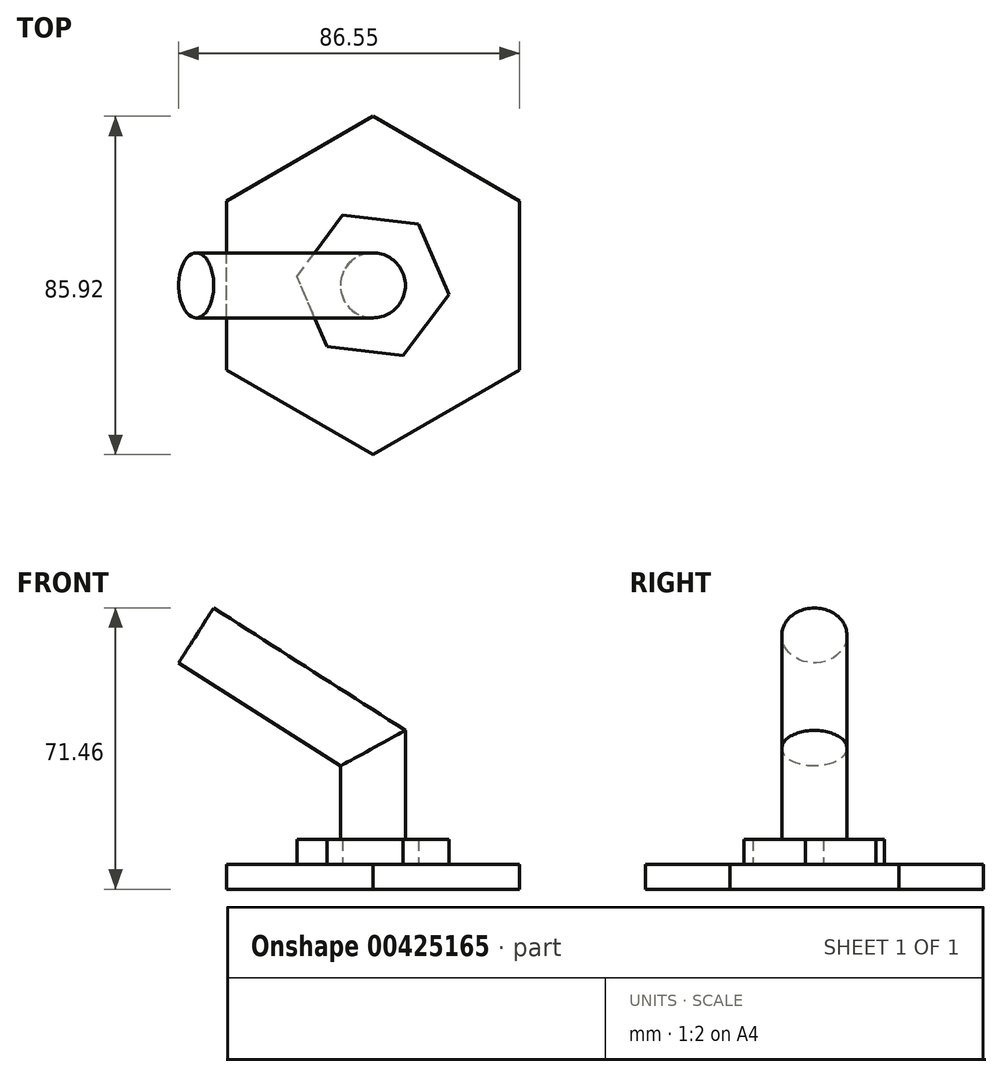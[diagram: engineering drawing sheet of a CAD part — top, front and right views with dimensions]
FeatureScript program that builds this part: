
annotation { "Feature Type Name" : "Feature", "Feature Type Description" : "" }
export const myFeature = defineFeature(function(context is Context, id is Id, definition is map)
    precondition{}
    {
        {
            var Q0;
            Q0=qCreatedBy(makeId("Top.planeOp"),FACE);
            var sketch = newSketch(context, id + "F0", { "sketchPlane" : qUnion([Q0])});
            skCircle(sketch, "E0.cCircle", {"center": v(0, 0) * mm, "radius": 37.2 * mm, "construction": true});
            skLineSegment(sketch, "E0.0", {"start": v(37.2, 21.48) * mm, "end": v(37.2, -21.48) * mm});
            skLineSegment(sketch, "E0.1", {"start": v(37.2, -21.48) * mm, "end": v(0, -42.96) * mm});
            skLineSegment(sketch, "E0.2", {"start": v(0, -42.96) * mm, "end": v(-37.2, -21.48) * mm});
            skLineSegment(sketch, "E0.3", {"start": v(-37.2, -21.48) * mm, "end": v(-37.2, 21.48) * mm});
            skLineSegment(sketch, "E0.4", {"start": v(-37.2, 21.48) * mm, "end": v(0, 42.96) * mm});
            skLineSegment(sketch, "E0.5", {"start": v(0, 42.96) * mm, "end": v(37.2, 21.48) * mm});
            skPoint(sketch, "E0.0.midPoint", {"position": v(37.2, 0) * mm});
            skSolve(sketch);
        }
        {
            var Q0;
            Q0 = qSketchRegion(id + "F0", true);
            extrude(context, id + "F1", {"entities" : qUnion([Q0]), "depth" : 6.35 * mm});
        }
        {
            var Q0;
            Q0=makeQuery(id+"F1.opExtrude","CAP_FACE",FACE,{"disambiguationData":[OSD([sQuery(id+"F0.wireOp",EDGE,"E0.0"),sQuery(id+"F0.wireOp",EDGE,"E0.1"),sQuery(id+"F0.wireOp",EDGE,"E0.2"),sQuery(id+"F0.wireOp",EDGE,"E0.3"),sQuery(id+"F0.wireOp",EDGE,"E0.4"),sQuery(id+"F0.wireOp",EDGE,"E0.5")])],"isStart":false});
            var sketch = newSketch(context, id + "F2", { "sketchPlane" : qUnion([Q0])});
            skCircle(sketch, "E1.cCircle", {"center": v(0, 0) * mm, "radius": 16.83 * mm, "construction": true});
            skLineSegment(sketch, "E1.0", {"start": v(11.62, 15.58) * mm, "end": v(19.3, -2.28) * mm});
            skLineSegment(sketch, "E1.1", {"start": v(19.3, -2.28) * mm, "end": v(7.68, -17.85) * mm});
            skLineSegment(sketch, "E1.2", {"start": v(7.68, -17.85) * mm, "end": v(-11.62, -15.58) * mm});
            skLineSegment(sketch, "E1.3", {"start": v(-11.62, -15.58) * mm, "end": v(-19.3, 2.28) * mm});
            skLineSegment(sketch, "E1.4", {"start": v(-19.3, 2.28) * mm, "end": v(-7.68, 17.85) * mm});
            skLineSegment(sketch, "E1.5", {"start": v(-7.68, 17.85) * mm, "end": v(11.62, 15.58) * mm});
            skPoint(sketch, "E1.0.midPoint", {"position": v(15.46, 6.65) * mm});
            skSolve(sketch);
        }
        {
            var Q0;
            Q0 = qSketchRegion(id + "F2", true);
            extrude(context, id + "F3", {"entities" : qUnion([Q0]), "operationType" : NewBodyOperationType.ADD, "depth" : 6.35 * mm});
        }
        {
            var Q0;
            Q0=qCreatedBy(makeId("Front.planeOp"),FACE);
            var sketch = newSketch(context, id + "F4", { "sketchPlane" : qUnion([Q0])});
            skLineSegment(sketch, "E2.0", {"start": v(7.68, 12.7) * mm, "end": v(-11.62, 12.7) * mm, "construction": true});
            skLineSegment(sketch, "E3", {"start": v(0, 12.7) * mm, "end": v(0, 35.81) * mm});
            skPoint(sketch, "E3.startSnap0", {"position": v(-1.97, 12.7) * mm});
            skLineSegment(sketch, "E4", {"start": v(0, 35.81) * mm, "end": v(-44.89, 64.5) * mm});
            skSolve(sketch);
        }
        {
            var Q0;
            Q0=makeQuery(id+"F3.opExtrude","CAP_FACE",FACE,{"disambiguationData":[OSD([sQuery(id+"F2.wireOp",EDGE,"E1.0"),sQuery(id+"F2.wireOp",EDGE,"E1.1"),sQuery(id+"F2.wireOp",EDGE,"E1.2"),sQuery(id+"F2.wireOp",EDGE,"E1.3"),sQuery(id+"F2.wireOp",EDGE,"E1.4"),sQuery(id+"F2.wireOp",EDGE,"E1.5")])],"isStart":false});
            var sketch = newSketch(context, id + "F5", { "sketchPlane" : qUnion([Q0])});
            skCircle(sketch, "E5", {"center": v(0, 0) * mm, "radius": 8.27 * mm});
            skSolve(sketch);
        }
        {
            var Q0;
            Q0=makeQuery(id+"F5.imprint","IMPRINT",FACE,{"disambiguationData":[TD([[makeQuery(id+"F5.imprint","IMPRINT",EDGE,{"derivedFrom":sQuery(id+"F5.wireOp",EDGE,"E5")}),1.0]])]});
            var Q1;
            Q1 = qConstructionFilter(qBodyType(qCreatedBy(id + "F4" ,EDGE), BodyType.WIRE), ConstructionObject.NO);
            sweep(context, id + "F6", {"profiles" : qUnion([Q0]), "path" : qUnion([Q1])});
        }
    });
